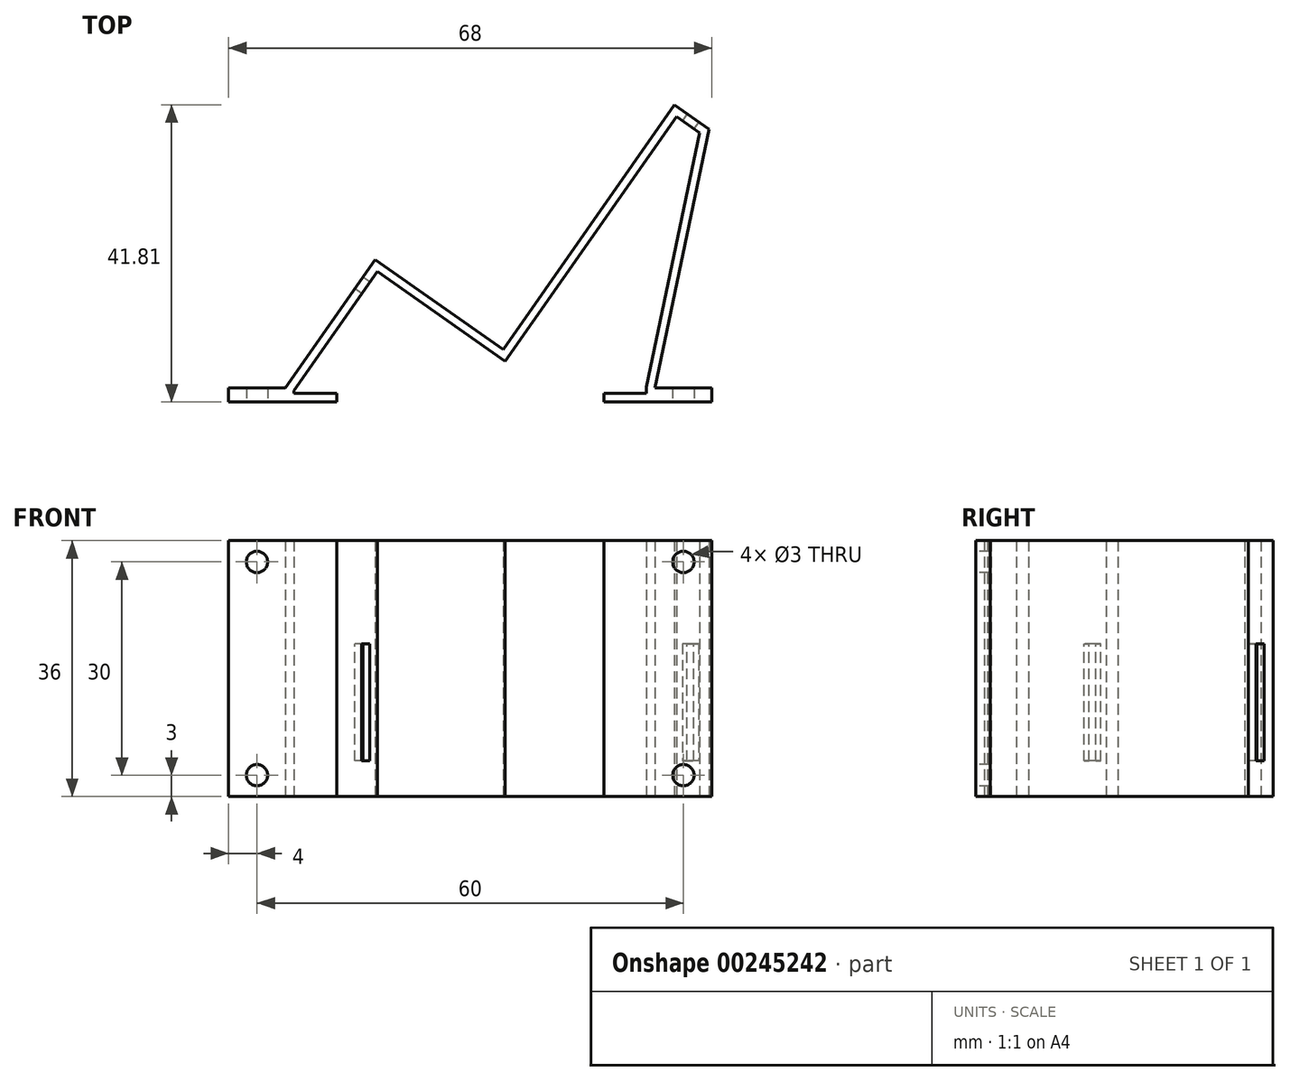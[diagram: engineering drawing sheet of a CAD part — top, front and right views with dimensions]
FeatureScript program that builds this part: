
annotation { "Feature Type Name" : "Feature", "Feature Type Description" : "" }
export const myFeature = defineFeature(function(context is Context, id is Id, definition is map)
    precondition{}
    {
        {
            var Q0;
            Q0=qCreatedBy(makeId("Top.planeOp"),FACE);
            var sketch = newSketch(context, id + "F0", { "sketchPlane" : qUnion([Q0])});
            skLineSegment(sketch, "E0.bottom", {"start": v(-35.8, 0) * mm, "end": v(24.2, 0) * mm, "construction": true});
            skLineSegment(sketch, "E0.top", {"start": v(-35.8, 50) * mm, "end": v(24.2, 50) * mm, "construction": true});
            skLineSegment(sketch, "E0.left", {"start": v(-35.8, 0) * mm, "end": v(-35.8, 50) * mm, "construction": true});
            skLineSegment(sketch, "E0.right", {"start": v(24.2, 0) * mm, "end": v(24.2, 50) * mm, "construction": true});
            skLineSegment(sketch, "E1", {"start": v(-35.8, 0) * mm, "end": v(-39.8, 0) * mm});
            skLineSegment(sketch, "E2", {"start": v(-39.8, 0) * mm, "end": v(-39.8, 2) * mm});
            skLineSegment(sketch, "E3", {"start": v(-39.8, 2) * mm, "end": v(-31.8, 2) * mm});
            skLineSegment(sketch, "E4", {"start": v(-31.8, 2) * mm, "end": v(-31.8, 20.38) * mm, "construction": true});
            skLineSegment(sketch, "E5", {"start": v(-31.8, 2) * mm, "end": v(-19.18, 20.02) * mm});
            skLineSegment(sketch, "E6", {"start": v(-19.18, 20.02) * mm, "end": v(-1.16, 7.4) * mm});
            skLineSegment(sketch, "E7", {"start": v(-1.16, 7.4) * mm, "end": v(22.93, 41.8) * mm});
            skLineSegment(sketch, "E8", {"start": v(22.93, 41.8) * mm, "end": v(27.85, 38.37) * mm});
            skLineSegment(sketch, "E9", {"start": v(24.2, 0) * mm, "end": v(28.2, 0) * mm});
            skLineSegment(sketch, "E10", {"start": v(28.2, 0) * mm, "end": v(28.2, 2) * mm});
            skLineSegment(sketch, "E11", {"start": v(28.2, 2) * mm, "end": v(24.2, 2) * mm});
            skLineSegment(sketch, "E12.bottom", {"start": v(24.2, 0) * mm, "end": v(20.2, 0) * mm});
            skLineSegment(sketch, "E12.top", {"start": v(24.2, 2) * mm, "end": v(20.2, 2) * mm});
            skLineSegment(sketch, "E12.left", {"start": v(24.2, 0) * mm, "end": v(24.2, 2) * mm});
            skLineSegment(sketch, "E12.right", {"start": v(20.2, 0) * mm, "end": v(20.2, 2) * mm});
            skLineSegment(sketch, "E13", {"start": v(27.85, 38.37) * mm, "end": v(20.2, 2) * mm});
            skLineSegment(sketch, "E14", {"start": v(-31.8, 2) * mm, "end": v(-31.8, 0) * mm});
            skLineSegment(sketch, "E15", {"start": v(-35.8, 0) * mm, "end": v(-31.8, 0) * mm});
            skLineSegment(sketch, "E16", {"start": v(-31.8, 0) * mm, "end": v(20.2, 0) * mm});
            skLineSegment(sketch, "E17.0", {"start": v(-30.6, 1.62) * mm, "end": v(-18.89, 18.35) * mm});
            skLineSegment(sketch, "E17.1", {"start": v(-30.6, 1.62) * mm, "end": v(-30.6, 1.2) * mm});
            skLineSegment(sketch, "E17.2", {"start": v(-18.89, 18.35) * mm, "end": v(-0.87, 5.73) * mm});
            skLineSegment(sketch, "E17.3", {"start": v(-30.6, 1.2) * mm, "end": v(19, 1.2) * mm});
            skLineSegment(sketch, "E17.4", {"start": v(-0.87, 5.73) * mm, "end": v(23.23, 40.14) * mm});
            skLineSegment(sketch, "E17.5", {"start": v(23.23, 40.14) * mm, "end": v(26.5, 37.84) * mm});
            skLineSegment(sketch, "E17.6", {"start": v(26.5, 37.84) * mm, "end": v(19, 2.12) * mm});
            skLineSegment(sketch, "E17.7", {"start": v(19, 1.2) * mm, "end": v(19, 2.12) * mm});
            skLineSegment(sketch, "E18", {"start": v(-30.6, 1.2) * mm, "end": v(-24.6, 1.2) * mm});
            skLineSegment(sketch, "E19", {"start": v(-24.6, 1.2) * mm, "end": v(-24.6, 0) * mm});
            skLineSegment(sketch, "E20", {"start": v(19, 1.2) * mm, "end": v(13, 1.2) * mm});
            skLineSegment(sketch, "E21", {"start": v(13, 1.2) * mm, "end": v(13, 0) * mm});
            skSolve(sketch);
        }
        {
            var Q0;
            Q0=makeQuery(id+"F0.imprint","IMPRINT",FACE,{"disambiguationData":[TD([[makeQuery(id+"F0.imprint","IMPRINT",EDGE,{"derivedFrom":sQuery(id+"F0.wireOp",EDGE,"E1")}),-1.0]])]});
            var Q1;
            Q1=makeQuery(id+"F0.imprint","IMPRINT",FACE,{"disambiguationData":[TD([[makeQuery(id+"F0.imprint","IMPRINT",EDGE,{"derivedFrom":sQuery(id+"F0.wireOp",EDGE,"E12.bottom")}),-1.0]])]});
            var Q2;
            Q2=makeQuery(id+"F0.imprint","IMPRINT",FACE,{"disambiguationData":[TD([[makeQuery(id+"F0.imprint","IMPRINT",EDGE,{"derivedFrom":sQuery(id+"F0.wireOp",EDGE,"E9")}),1.0]])]});
            var Q3;
            Q3=makeQuery(id+"F0.imprint","IMPRINT",FACE,{"disambiguationData":[TD([[makeQuery(id+"F0.imprint","IMPRINT",EDGE,{"derivedFrom":sQuery(id+"F0.wireOp",EDGE,"E5")}),-1.0]])]});
            extrude(context, id + "F1", {"entities" : qUnion([Q0, Q1, Q2, Q3]), "depth" : 36 * mm});
        }
        {
            var Q0;
            Q0=makeQuery(id+"F0.imprint","IMPRINT",FACE,{"disambiguationData":[TD([[makeQuery(id+"F0.imprint","IMPRINT",EDGE,{"derivedFrom":sQuery(id+"F0.wireOp",EDGE,"E17.3")}),-1.0]])]});
            extrude(context, id + "F2", {"entities" : qUnion([Q0]), "operationType" : NewBodyOperationType.REMOVE, "oppositeDirection" : true, "depth" : 36 * mm});
        }
        {
            var Q0;
            Q0=makeQuery(id+"F1.opExtrude","SWEPT_FACE",FACE,{"disambiguationData":[OSD([sQuery(id+"F0.wireOp",EDGE,"E1"),sQuery(id+"F0.wireOp",EDGE,"E15"),sQuery(id+"F0.wireOp",EDGE,"E16")])]});
            var sketch = newSketch(context, id + "F3", { "sketchPlane" : qUnion([Q0])});
            skLineSegment(sketch, "E22.bottom", {"start": v(-39.8, 0) * mm, "end": v(28.2, 0) * mm});
            skLineSegment(sketch, "E22.top", {"start": v(-39.8, 36) * mm, "end": v(28.2, 36) * mm});
            skLineSegment(sketch, "E22.left", {"start": v(-39.8, 0) * mm, "end": v(-39.8, 36) * mm});
            skLineSegment(sketch, "E22.right", {"start": v(28.2, 0) * mm, "end": v(28.2, 36) * mm});
            skLineSegment(sketch, "E23.bottom", {"start": v(-39.8, 0) * mm, "end": v(-35.8, 0) * mm});
            skLineSegment(sketch, "E23.top", {"start": v(-39.8, 3) * mm, "end": v(-35.8, 3) * mm, "construction": true});
            skLineSegment(sketch, "E23.left", {"start": v(-39.8, 0) * mm, "end": v(-39.8, 3) * mm});
            skLineSegment(sketch, "E23.right", {"start": v(-35.8, 0) * mm, "end": v(-35.8, 3) * mm, "construction": true});
            skLineSegment(sketch, "E24.bottom", {"start": v(-39.8, 36) * mm, "end": v(-35.8, 36) * mm});
            skLineSegment(sketch, "E24.top", {"start": v(-39.8, 33) * mm, "end": v(-35.8, 33) * mm, "construction": true});
            skLineSegment(sketch, "E24.left", {"start": v(-39.8, 36) * mm, "end": v(-39.8, 33) * mm});
            skLineSegment(sketch, "E24.right", {"start": v(-35.8, 36) * mm, "end": v(-35.8, 33) * mm, "construction": true});
            skLineSegment(sketch, "E25.bottom", {"start": v(-35.8, 33) * mm, "end": v(24.2, 33) * mm, "construction": true});
            skLineSegment(sketch, "E25.top", {"start": v(-35.8, 3) * mm, "end": v(24.2, 3) * mm, "construction": true});
            skLineSegment(sketch, "E25.left", {"start": v(-35.8, 33) * mm, "end": v(-35.8, 3) * mm, "construction": true});
            skLineSegment(sketch, "E25.right", {"start": v(24.2, 33) * mm, "end": v(24.2, 3) * mm, "construction": true});
            skCircle(sketch, "E26", {"center": v(24.2, 33) * mm, "radius": 1.5 * mm});
            skCircle(sketch, "E27", {"center": v(24.2, 3) * mm, "radius": 1.5 * mm});
            skCircle(sketch, "E28", {"center": v(-35.8, 33) * mm, "radius": 1.5 * mm});
            skCircle(sketch, "E29", {"center": v(-35.8, 3) * mm, "radius": 1.5 * mm});
            skSolve(sketch);
        }
        {
            var Q0;
            Q0=makeQuery(id+"F3.imprint","IMPRINT",FACE,{"disambiguationData":[TD([[makeQuery(id+"F3.imprint","IMPRINT",EDGE,{"derivedFrom":sQuery(id+"F3.wireOp",EDGE,"E28")}),1.0]])]});
            var Q1;
            Q1=makeQuery(id+"F3.imprint","IMPRINT",FACE,{"disambiguationData":[TD([[makeQuery(id+"F3.imprint","IMPRINT",EDGE,{"derivedFrom":sQuery(id+"F3.wireOp",EDGE,"E26")}),1.0]])]});
            var Q2;
            Q2=makeQuery(id+"F3.imprint","IMPRINT",FACE,{"disambiguationData":[TD([[makeQuery(id+"F3.imprint","IMPRINT",EDGE,{"derivedFrom":sQuery(id+"F3.wireOp",EDGE,"E27")}),1.0]])]});
            var Q3;
            Q3=makeQuery(id+"F3.imprint","IMPRINT",FACE,{"disambiguationData":[TD([[makeQuery(id+"F3.imprint","IMPRINT",EDGE,{"derivedFrom":sQuery(id+"F3.wireOp",EDGE,"E29")}),1.0]])]});
            extrude(context, id + "F4", {"entities" : qUnion([Q0, Q1, Q2, Q3]), "operationType" : NewBodyOperationType.REMOVE, "oppositeDirection" : true, "depth" : 3 * mm});
        }
        {
            var Q0;
            Q0=makeQuery(id+"F1.opExtrude","SWEPT_FACE",FACE,{"disambiguationData":[OSD([sQuery(id+"F0.wireOp",EDGE,"E5")])]});
            var sketch = newSketch(context, id + "F5", { "sketchPlane" : qUnion([Q0])});
            skLineSegment(sketch, "E30.bottom", {"start": v(-5.4, 0) * mm, "end": v(-2.4, 0) * mm});
            skLineSegment(sketch, "E30.top", {"start": v(-5.4, 5) * mm, "end": v(-2.4, 5) * mm});
            skLineSegment(sketch, "E30.left", {"start": v(-5.4, 0) * mm, "end": v(-5.4, 5) * mm});
            skLineSegment(sketch, "E30.right", {"start": v(-2.4, 0) * mm, "end": v(-2.4, 5) * mm});
            skLineSegment(sketch, "E31.bottom", {"start": v(-2.4, 5) * mm, "end": v(-0.4, 5) * mm});
            skLineSegment(sketch, "E31.top", {"start": v(-2.4, 21.5) * mm, "end": v(-0.4, 21.5) * mm});
            skLineSegment(sketch, "E31.left", {"start": v(-2.4, 5) * mm, "end": v(-2.4, 21.5) * mm});
            skLineSegment(sketch, "E31.right", {"start": v(-0.4, 5) * mm, "end": v(-0.4, 21.5) * mm});
            skSolve(sketch);
        }
        {
            var Q0;
            Q0=makeQuery(id+"F5.imprint","IMPRINT",FACE,{"disambiguationData":[TD([[makeQuery(id+"F5.imprint","IMPRINT",EDGE,{"derivedFrom":sQuery(id+"F5.wireOp",EDGE,"E31.bottom")}),1.0]])]});
            extrude(context, id + "F6", {"entities" : qUnion([Q0]), "operationType" : NewBodyOperationType.REMOVE, "oppositeDirection" : true, "depth" : 2 * mm});
        }
        {
            var Q0;
            Q0=makeQuery(id+"F1.opExtrude","SWEPT_FACE",FACE,{"disambiguationData":[OSD([sQuery(id+"F0.wireOp",EDGE,"E17.5")])]});
            var sketch = newSketch(context, id + "F7", { "sketchPlane" : qUnion([Q0])});
            skLineSegment(sketch, "E32", {"start": v(-2, 0) * mm, "end": v(-2, 5) * mm});
            skLineSegment(sketch, "E33", {"start": v(-2, 5) * mm, "end": v(-1, 5) * mm});
            skLineSegment(sketch, "E34", {"start": v(-1, 5) * mm, "end": v(-1, 21.5) * mm});
            skLineSegment(sketch, "E35", {"start": v(-1, 21.5) * mm, "end": v(-3, 21.5) * mm});
            skLineSegment(sketch, "E36", {"start": v(-3, 21.5) * mm, "end": v(-3, 5) * mm});
            skLineSegment(sketch, "E37", {"start": v(-3, 5) * mm, "end": v(-2, 5) * mm});
            skSolve(sketch);
        }
        {
            var Q0;
            Q0=makeQuery(id+"F7.imprint","IMPRINT",FACE,{"disambiguationData":[TD([[makeQuery(id+"F7.imprint","IMPRINT",EDGE,{"derivedFrom":sQuery(id+"F7.wireOp",EDGE,"E33")}),1.0]])]});
            extrude(context, id + "F8", {"entities" : qUnion([Q0]), "operationType" : NewBodyOperationType.REMOVE, "oppositeDirection" : true, "depth" : 25 * mm});
        }
    });
